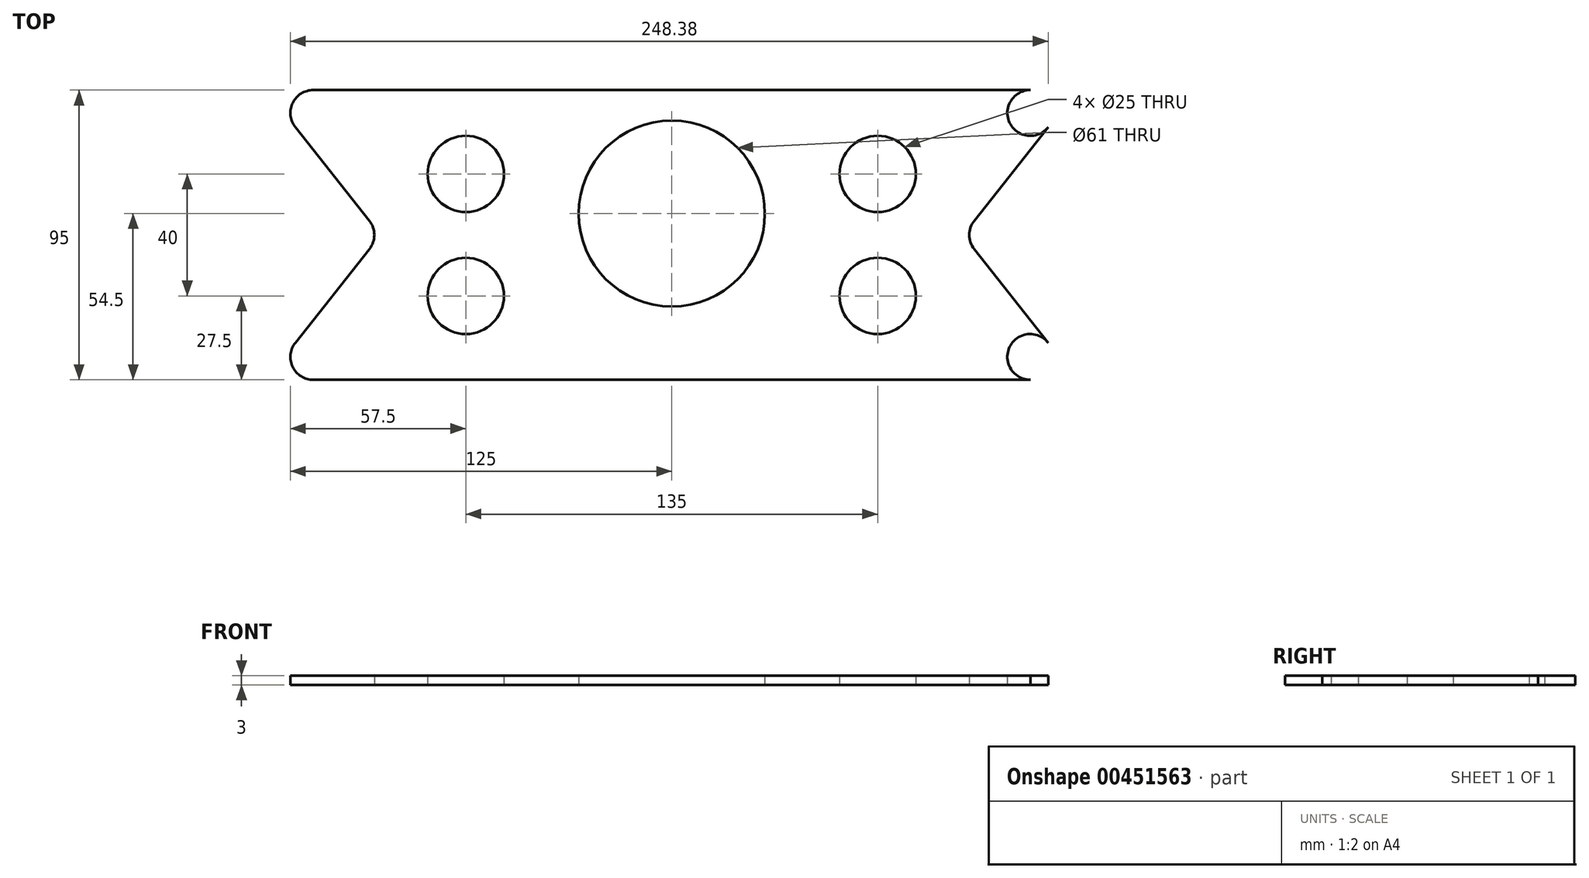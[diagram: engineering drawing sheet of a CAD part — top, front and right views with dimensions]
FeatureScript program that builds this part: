
annotation { "Feature Type Name" : "Feature", "Feature Type Description" : "" }
export const myFeature = defineFeature(function(context is Context, id is Id, definition is map)
    precondition{}
    {
        {
            var Q0;
            Q0=qCreatedBy(makeId("Top.planeOp"),FACE);
            var sketch = newSketch(context, id + "F0", { "sketchPlane" : qUnion([Q0])});
            skCircle(sketch, "E0", {"center": v(0, 0) * mm, "radius": 30.5 * mm});
            skLineSegment(sketch, "E1.bottom", {"start": v(-125, -54.5) * mm, "end": v(125, -54.5) * mm});
            skLineSegment(sketch, "E1.top", {"start": v(-125, 40.5) * mm, "end": v(125, 40.5) * mm});
            skLineSegment(sketch, "E1.left", {"start": v(-125, -54.5) * mm, "end": v(-125, 40.5) * mm});
            skLineSegment(sketch, "E1.right", {"start": v(125, -54.5) * mm, "end": v(125, 40.5) * mm});
            skCircle(sketch, "E2", {"center": v(-67.5, 13) * mm, "radius": 12.5 * mm});
            skCircle(sketch, "E3", {"center": v(-67.5, -27) * mm, "radius": 12.5 * mm});
            skCircle(sketch, "E4.MirrorC", {"center": v(67.5, 13) * mm, "radius": 12.5 * mm});
            skCircle(sketch, "E5.MirrorC", {"center": v(67.5, -27) * mm, "radius": 12.5 * mm});
            skCircle(sketch, "E6", {"center": v(-105, -7) * mm, "radius": 7.5 * mm});
            skCircle(sketch, "E7", {"center": v(-117.5, -47) * mm, "radius": 7.5 * mm});
            skCircle(sketch, "E8", {"center": v(-117.5, 33) * mm, "radius": 7.5 * mm});
            skLineSegment(sketch, "E9", {"start": v(-123.38, 28.35) * mm, "end": v(-99.12, -2.35) * mm});
            skLineSegment(sketch, "E10", {"start": v(-99.12, -11.65) * mm, "end": v(-123.38, -42.35) * mm});
            skCircle(sketch, "E11.MirrorC", {"center": v(117.5, 33) * mm, "radius": 7.5 * mm});
            skLineSegment(sketch, "E12.MirrorCS", {"start": v(123.38, 28.35) * mm, "end": v(99.12, -2.35) * mm});
            skCircle(sketch, "E13.MirrorC", {"center": v(105, -7) * mm, "radius": 7.5 * mm});
            skLineSegment(sketch, "E14.MirrorCS", {"start": v(99.12, -11.65) * mm, "end": v(123.38, -42.35) * mm});
            skCircle(sketch, "E15.MirrorC", {"center": v(117.5, -47) * mm, "radius": 7.5 * mm});
            skSolve(sketch);
        }
        {
            var Q0;
            Q0=makeQuery(id+"F0.imprint","IMPRINT",FACE,{"disambiguationData":[TD([[makeQuery(id+"F0.imprint","IMPRINT",EDGE,{"derivedFrom":sQuery(id+"F0.wireOp",EDGE,"E0")}),-1.0]])]});
            var Q1;
            {var subQ0=sQuery(id+"F0.wireOp",EDGE,"E8");var subQ1=makeQuery(id+"F0.imprint","INTERSECT",VERTEX,{"derivedFrom":[sQuery(id+"F0.wireOp",EDGE,"E1.top"),subQ0]});Q1=makeQuery(id+"F0.imprint","IMPRINT",FACE,{"disambiguationData":[TD([[makeQuery(id+"F0.imprint","IMPRINT",EDGE,{"disambiguationData":[TD([[subQ1,-1.0]])],"derivedFrom":subQ0}),1.0]])]});}
            var Q2;
            {var subQ0=sQuery(id+"F0.wireOp",EDGE,"E7");var subQ1=makeQuery(id+"F0.imprint","INTERSECT",VERTEX,{"derivedFrom":[subQ0,sQuery(id+"F0.wireOp",EDGE,"E10")]});Q2=makeQuery(id+"F0.imprint","IMPRINT",FACE,{"disambiguationData":[TD([[makeQuery(id+"F0.imprint","IMPRINT",EDGE,{"disambiguationData":[TD([[subQ1,-1.0]])],"derivedFrom":subQ0}),1.0]])]});}
            var Q3;
            {var subQ0=sQuery(id+"F0.wireOp",EDGE,"E15.MirrorC");var subQ1=makeQuery(id+"F0.imprint","INTERSECT",VERTEX,{"derivedFrom":[sQuery(id+"F0.wireOp",EDGE,"E14.MirrorCS"),subQ0]});Q3=makeQuery(id+"F0.imprint","IMPRINT",FACE,{"disambiguationData":[TD([[makeQuery(id+"F0.imprint","IMPRINT",EDGE,{"disambiguationData":[TD([[subQ1,-1.0]])],"derivedFrom":subQ0}),-1.0]])]});}
            var Q4;
            {var subQ0=sQuery(id+"F0.wireOp",EDGE,"E11.MirrorC");var subQ1=makeQuery(id+"F0.imprint","INTERSECT",VERTEX,{"derivedFrom":[sQuery(id+"F0.wireOp",EDGE,"E1.top"),subQ0]});Q4=makeQuery(id+"F0.imprint","IMPRINT",FACE,{"disambiguationData":[TD([[makeQuery(id+"F0.imprint","IMPRINT",EDGE,{"disambiguationData":[TD([[subQ1,-1.0]])],"derivedFrom":subQ0}),-1.0]])]});}
            extrude(context, id + "F1", {"entities" : qUnion([Q0, Q1, Q2, Q3, Q4]), "depth" : 3 * mm, "offsetDistance" : 25 * mm});
        }
    });
